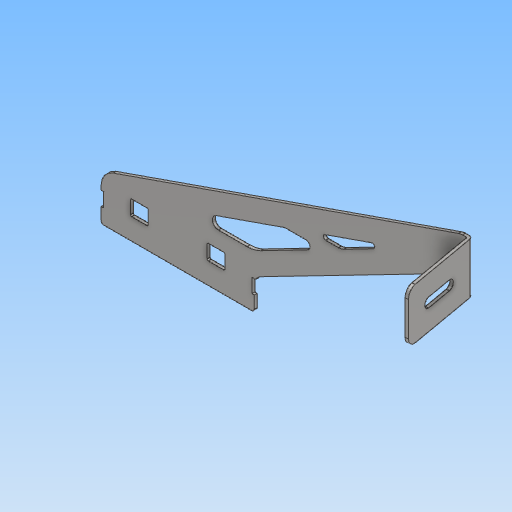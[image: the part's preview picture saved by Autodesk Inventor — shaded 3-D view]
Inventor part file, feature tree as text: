
AUTODESK INVENTOR PART (.ipt)
format: ipt  version: 2020 (Build 240168000, 168)  size: 221,184 bytes
history: native  units: mm
features: other x4, sketch x1, plane x1
ambient origin geometry x8: Origin, YZ Plane, XZ Plane, XY Plane, X Axis, Y Axis, Z Axis, Center Point
bodies: Body1 (feature_tree)
feature tree (6):
  other  "白鐵-吊架-長(R).ipt"
  other  "實體1::白鐵-吊架-長(R).ipt"
  other  "標籤特徵1"
  sketch  "草圖1"
  plane  "工作平面1"
  other  "實體1"
